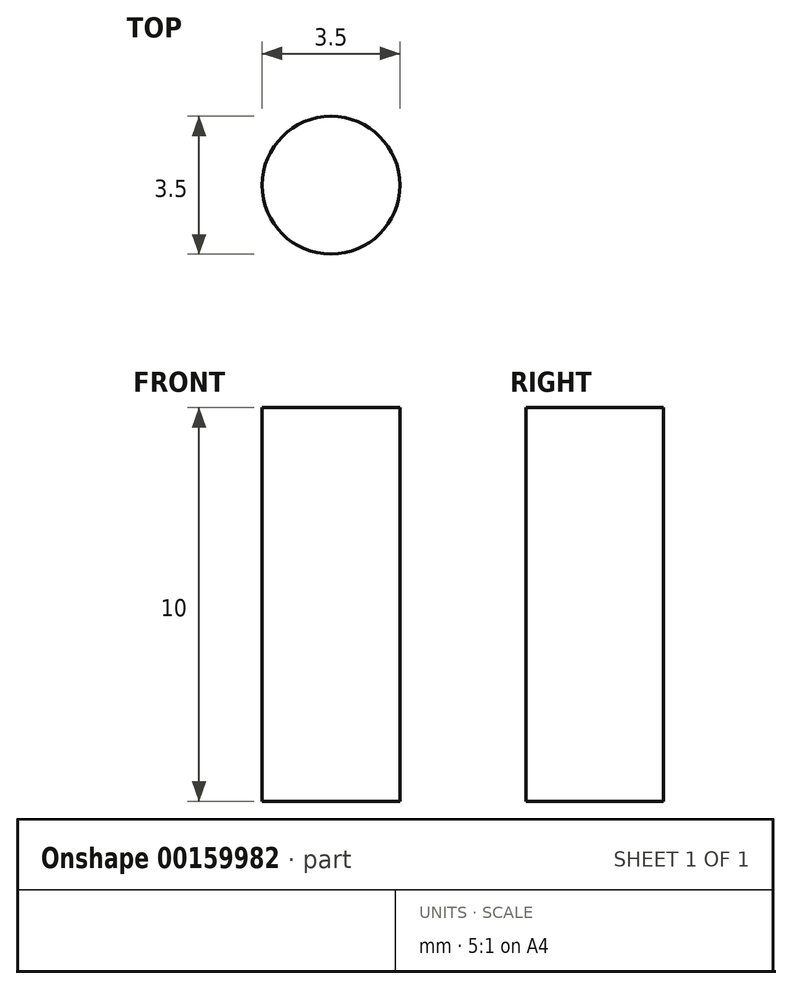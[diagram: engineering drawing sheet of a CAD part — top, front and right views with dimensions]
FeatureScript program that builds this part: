
annotation { "Feature Type Name" : "Feature", "Feature Type Description" : "" }
export const myFeature = defineFeature(function(context is Context, id is Id, definition is map)
    precondition{}
    {
        {
            var Q0;
            Q0=qCreatedBy(makeId("Top.planeOp"),FACE);
            var sketch = newSketch(context, id + "F0", { "sketchPlane" : qUnion([Q0])});
            skCircle(sketch, "E0", {"center": v(0, 0) * mm, "radius": 1.75 * mm});
            skSolve(sketch);
        }
        {
            var Q0;
            Q0 = qSketchRegion(id + "F0", true);
            extrude(context, id + "F1", {"entities" : qUnion([Q0]), "depth" : 10 * mm});
        }
    });
